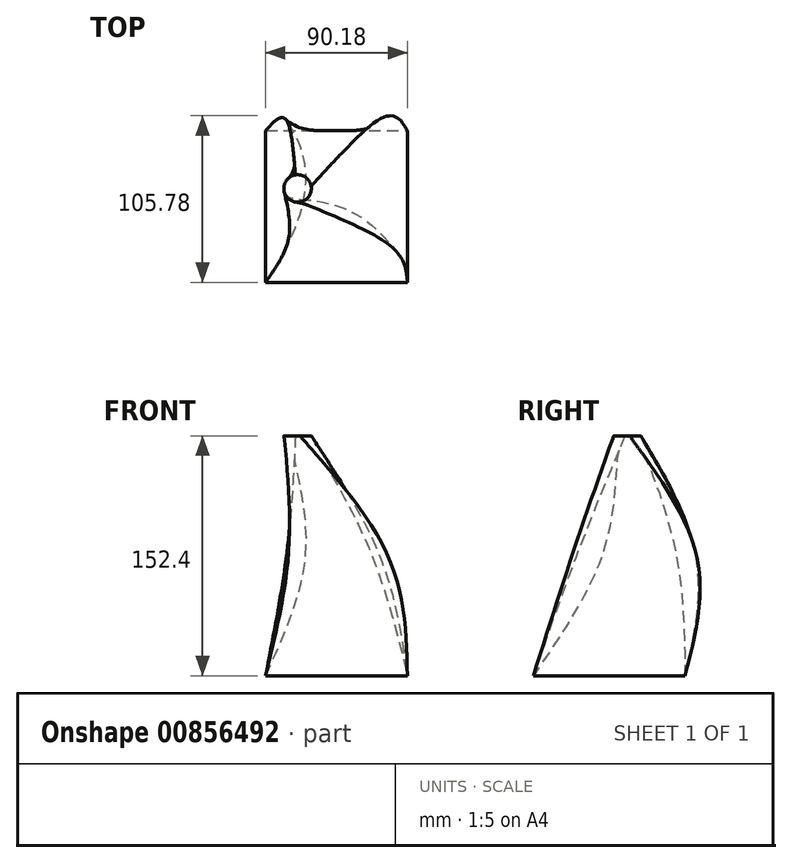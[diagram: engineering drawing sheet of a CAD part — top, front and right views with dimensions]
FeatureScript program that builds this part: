
annotation { "Feature Type Name" : "Feature", "Feature Type Description" : "" }
export const myFeature = defineFeature(function(context is Context, id is Id, definition is map)
    precondition{}
    {
        {
            var Q0;
            Q0=qCreatedBy(makeId("Top.planeOp"),FACE);
            cPlane(context, id + "F0", {"entities" : qUnion([Q0]), "cplaneType" : CPlaneType.OFFSET, "offset" : 76.2 * mm, "width" : 152.4 * mm, "height" : 152.4 * mm});
        }
        {
            var Q0;
            Q0=qCreatedBy(id+"F0.planeOp",FACE);
            cPlane(context, id + "F1", {"entities" : qUnion([Q0]), "cplaneType" : CPlaneType.OFFSET, "offset" : 76.2 * mm, "width" : 152.4 * mm, "height" : 152.4 * mm});
        }
        {
            var Q0;
            Q0=qCreatedBy(makeId("Top.planeOp"),FACE);
            var sketch = newSketch(context, id + "F2", { "sketchPlane" : qUnion([Q0])});
            skLineSegment(sketch, "E0.bottom", {"start": v(-45.2, 36.8) * mm, "end": v(44.98, 36.8) * mm});
            skLineSegment(sketch, "E0.top", {"start": v(-45.2, -59.6) * mm, "end": v(44.98, -59.6) * mm});
            skLineSegment(sketch, "E0.left", {"start": v(-45.2, 36.8) * mm, "end": v(-45.2, -59.6) * mm});
            skLineSegment(sketch, "E0.right", {"start": v(44.98, 36.8) * mm, "end": v(44.98, -59.6) * mm});
            skSolve(sketch);
        }
        {
            var Q0;
            Q0=qCreatedBy(id+"F0.planeOp",FACE);
            var sketch = newSketch(context, id + "F3", { "sketchPlane" : qUnion([Q0])});
            skArc(sketch, "E1", {"start": v(-31.9, 43.34) * mm, "mid": v(-2.14, 31.2) * mm, "end": v(27.34, 43.98) * mm});
            skArc(sketch, "E2", {"start": v(32.5, -35.1) * mm, "mid": v(1.72, -16.1) * mm, "end": v(-30.63, -32.28) * mm});
            skArc(sketch, "E3", {"start": v(27.34, 43.98) * mm, "mid": v(22.7, 3.97) * mm, "end": v(32.5, -35.1) * mm});
            skArc(sketch, "E4", {"start": v(-30.63, -32.28) * mm, "mid": v(-19.93, 5.72) * mm, "end": v(-31.9, 43.34) * mm});
            skSolve(sketch);
        }
        {
            var Q0;
            Q0=qCreatedBy(id+"F1.planeOp",FACE);
            var sketch = newSketch(context, id + "F4", { "sketchPlane" : qUnion([Q0])});
            skCircle(sketch, "E5", {"center": v(-24.78, 0) * mm, "radius": 8.74 * mm});
            skSolve(sketch);
        }
        {
            var Q0;
            Q0=makeQuery(id+"F4.imprint","IMPRINT",FACE,{"disambiguationData":[TD([[makeQuery(id+"F4.imprint","IMPRINT",EDGE,{"derivedFrom":sQuery(id+"F4.wireOp",EDGE,"E5")}),1.0]])]});
            var Q1;
            Q1=makeQuery(id+"F3.imprint","IMPRINT",FACE,{"disambiguationData":[TD([[makeQuery(id+"F3.imprint","IMPRINT",EDGE,{"derivedFrom":sQuery(id+"F3.wireOp",EDGE,"E1")}),-1.0]])]});
            var Q2;
            Q2=makeQuery(id+"F2.imprint","IMPRINT",FACE,{"disambiguationData":[TD([[makeQuery(id+"F2.imprint","IMPRINT",EDGE,{"derivedFrom":sQuery(id+"F2.wireOp",EDGE,"E0.bottom")}),-1.0]])]});
            loft(context, id + "F5", {"sheetProfilesArray" : [{ "sheetProfileEntities" : qUnion([Q0]) }, { "sheetProfileEntities" : qUnion([Q1]) }, { "sheetProfileEntities" : qUnion([Q2]) }]});
        }
    });
